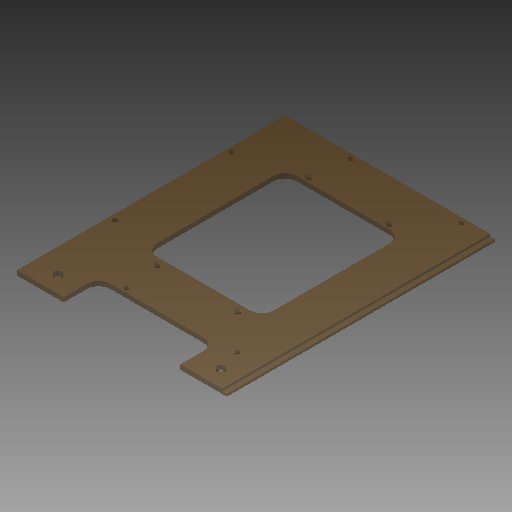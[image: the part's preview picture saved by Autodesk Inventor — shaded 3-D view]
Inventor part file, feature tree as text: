
AUTODESK INVENTOR PART (.ipt)
format: ipt  version: 2018 (Build 220112000, 112)  size: 182,272 bytes
history: native  units: mm
features: extrude x4, reference x4, hole x3, fillet x2
ambient origin geometry x8: Origin, YZ Plane, XZ Plane, XY Plane, X Axis, Y Axis, Z Axis, Center Point
bodies: Volumenkörper1 (feature_tree)
feature tree (13):
  extrude  "Extrusion1"  Depth=230.0mm
  hole  "Bohrung1"  [1 undecoded]
  extrude  "Extrusion2"  Depth=4.0mm TaperAngle=0.0deg
  extrude  "Extrusion3"  Depth=20.0mm
  fillet  "Rundung1"  Radius=20.0mm
  extrude  "Extrusion4"  Depth=15.0mm
  fillet  "Rundung2"  Radius=15.0mm
  hole  "Bohrung2"  [1 undecoded]
  hole  "Bohrung3"  [1 undecoded]
  reference  "Referenz1"
  reference  "Referenz2"
  reference  "Referenz3"
  reference  "Referenz4"
note: 3 required parameter values undecoded (feature->parameter linkage not recoverable at this tier; creation-order binding heuristic only, values carry confidence <= 0.55)
